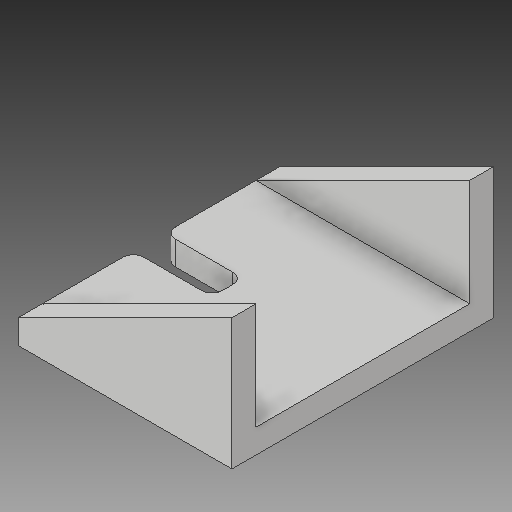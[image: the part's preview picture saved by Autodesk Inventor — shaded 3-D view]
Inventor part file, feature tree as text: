
AUTODESK INVENTOR PART (.ipt)
format: ipt  version: 2018 (Build 220112000, 112)  size: 144,896 bytes
history: native  units: mm
features: extrude x5, sketch x5, other x1, fillet x1
ambient origin geometry x8: Origin, YZ Plane, XZ Plane, XY Plane, X Axis, Y Axis, Z Axis, Center Point
bodies: Body1 (feature_tree)
feature tree (12):
  other  "ソリッド1"
  extrude  "押し出し1"  Depth=25.0mm
  extrude  "押し出し2"  Depth=25.0mm
  extrude  "押し出し3"  Depth=2.3mm
  extrude  "押し出し4"  Depth=25.0mm TaperAngle=0.0deg
  extrude  "押し出し5"  Depth=10.0mm TaperAngle=0.0deg
  fillet  "フィレット1"  Radius=10.0mm
  sketch  "スケッチ1"
  sketch  "スケッチ2"
  sketch  "スケッチ3"
  sketch  "スケッチ4"
  sketch  "スケッチ5"
